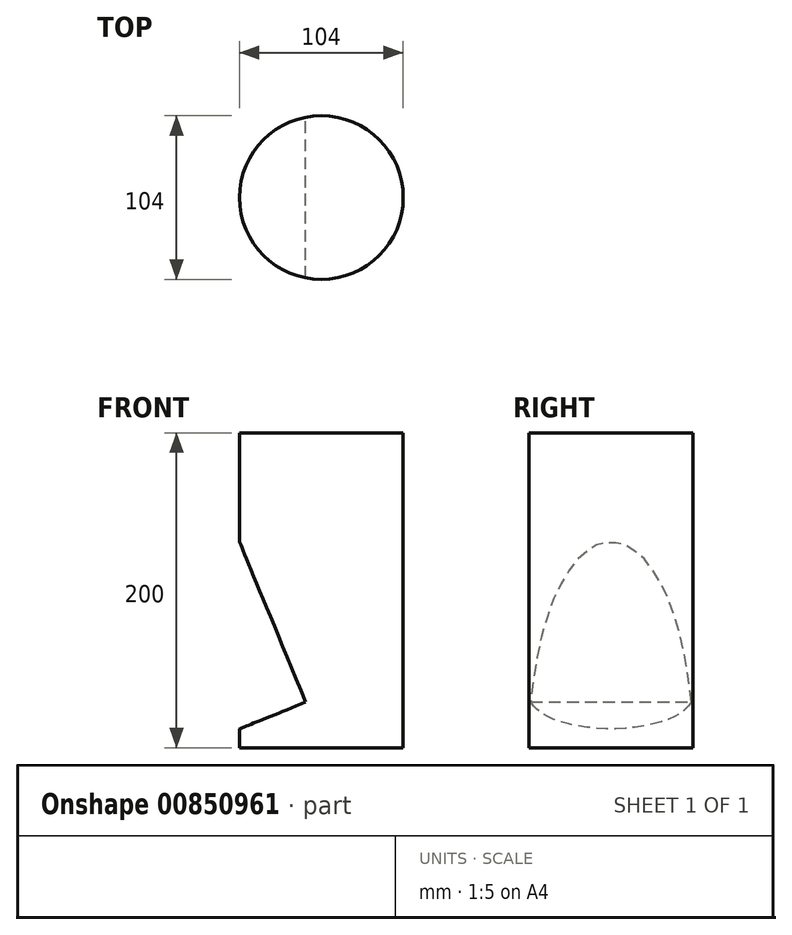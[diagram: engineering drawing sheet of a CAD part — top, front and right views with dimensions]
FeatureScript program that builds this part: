
annotation { "Feature Type Name" : "Feature", "Feature Type Description" : "" }
export const myFeature = defineFeature(function(context is Context, id is Id, definition is map)
    precondition{}
    {
        {
            var Q0;
            Q0=qCreatedBy(makeId("Top.planeOp"),FACE);
            var sketch = newSketch(context, id + "F0", { "sketchPlane" : qUnion([Q0])});
            skCircle(sketch, "E0", {"center": v(0, 0) * mm, "radius": 52 * mm});
            skSolve(sketch);
        }
        {
            var Q0;
            Q0=makeQuery(id+"F0.imprint","IMPRINT",FACE,{"disambiguationData":[TD([[makeQuery(id+"F0.imprint","IMPRINT",EDGE,{"derivedFrom":sQuery(id+"F0.wireOp",EDGE,"E0")}),1.0]])]});
            extrude(context, id + "F1", {"entities" : qUnion([Q0]), "depth" : 200 * mm, "offsetDistance" : 25 * mm});
        }
        {
            var Q0;
            Q0=qCreatedBy(makeId("Front.planeOp"),FACE);
            var sketch = newSketch(context, id + "F2", { "sketchPlane" : qUnion([Q0])});
            skLineSegment(sketch, "E1", {"start": v(-52, 12) * mm, "end": v(-10, 29) * mm});
            skLineSegment(sketch, "E2", {"start": v(-52, 12) * mm, "end": v(-52, 131) * mm});
            skLineSegment(sketch, "E3", {"start": v(-52, 131) * mm, "end": v(-10, 29) * mm});
            skSolve(sketch);
        }
        {
            var Q0;
            Q0 = qSketchRegion(id + "F2", true);
            extrude(context, id + "F3", {"entities" : qUnion([Q0]), "operationType" : NewBodyOperationType.REMOVE, "endBound" : BoundingType.SYMMETRIC, "depth" : 104 * mm, "offsetDistance" : 25 * mm});
        }
    });
